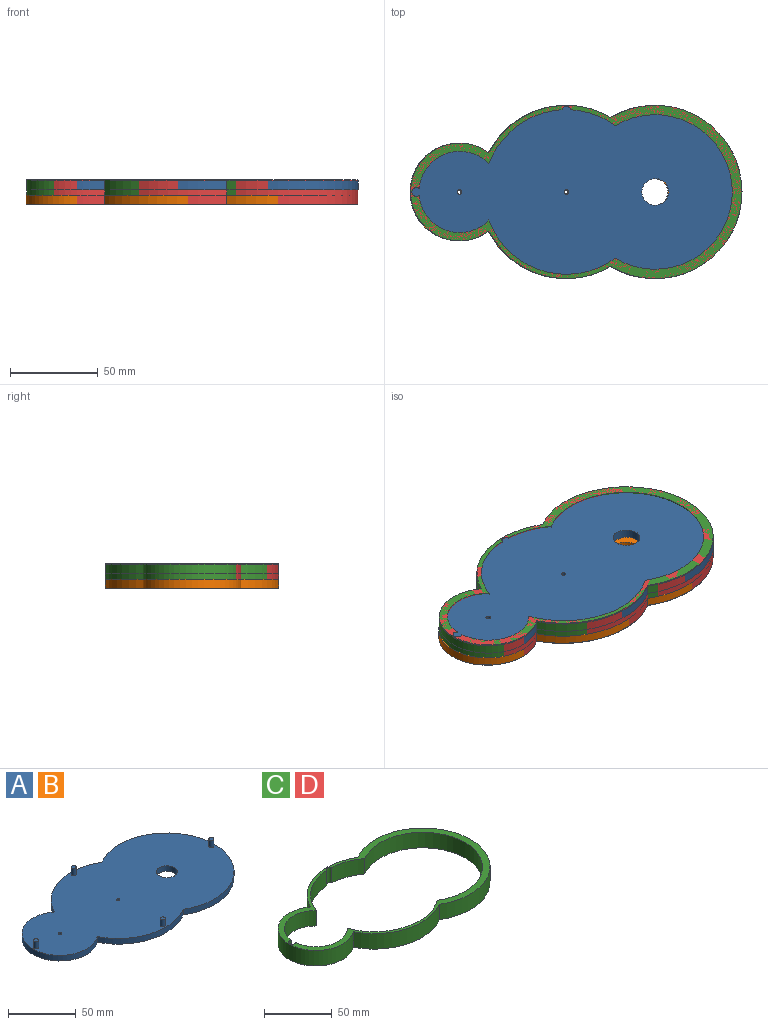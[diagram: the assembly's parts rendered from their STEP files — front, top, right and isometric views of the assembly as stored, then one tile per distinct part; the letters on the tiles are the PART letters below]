
ASSEMBLY  parts=4 mates=1
PART A: 17 faces, bbox 189.2x99.1x11.4 mm
  f0: cylinder r=27.94mm len=55.88mm, axis (0,0,-1), area 628.5mm2, adj f1,f6,f7,f8
  f1: cylinder r=49.53mm len=69.6mm, axis (0,0,-1), area 412.9mm2, adj f0,f2,f7,f8
  f2: cylinder r=49.53mm len=99.06mm, axis (0,0,-1), area 1061.4mm2, adj f1,f6,f7,f8
  f3: cylinder r=7.62mm len=15.24mm, axis (0,0,-1), area 243.2mm2, adj f7,f8
  f4: cylinder r=1.27mm len=5.08mm, axis (0,0,-1), area 40.5mm2, adj f7,f8
  f5: cylinder r=1.27mm len=5.08mm, axis (0,0,-1), area 40.5mm2, adj f7,f8
  f6: cylinder r=49.53mm len=69.6mm, axis (0,0,-1), area 412.9mm2, adj f0,f2,f7,f8
  f7: plane 189.23x99.06mm, normal (0,0,1), area 14213.4mm2, adj f0,f1,f2,f3,f4,f5,f6,f9
  f8: plane 189.23x99.06mm, normal (0,0,-1), area 14259mm2, adj f0,f1,f2,f3,f4,f5,f6
  f9: cylinder r=1.91mm len=6.35mm, axis (0,0,-1), area 76mm2, adj f7,f10
  f10: plane 3.81x3.81mm, normal (0,0,1), area 11.4mm2, adj f9
  f11: cylinder r=1.91mm len=6.35mm, axis (0,0,-1), area 76mm2, adj f7,f12
  f12: plane 3.81x3.81mm, normal (0,0,1), area 11.4mm2, adj f11
  f13: cylinder r=1.91mm len=6.35mm, axis (0,0,-1), area 76mm2, adj f7,f14
  f14: plane 3.81x3.81mm, normal (0,0,1), area 11.4mm2, adj f13
  f15: cylinder r=1.91mm len=6.35mm, axis (0,0,-1), area 76mm2, adj f7,f16
  f16: plane 3.81x3.81mm, normal (0,0,1), area 11.4mm2, adj f15
PART B: same geometry as A
PART C: 14 faces, bbox 189.2x99.1x14 mm
  f0: cylinder r=49.53mm len=69.6mm, axis (0,0,-1), area 1135.5mm2, adj f1,f11,f12,f13
  f1: cylinder r=27.94mm len=55.88mm, axis (0,0,-1), area 1728.5mm2, adj f0,f2,f12,f13
  f2: cylinder r=49.53mm len=69.6mm, axis (0,0,-1), area 1135.5mm2, adj f1,f11,f12,f13
  f3: cylinder r=47.03mm len=72.17mm, axis (0,0,-1), area 1221.9mm2, adj f4,f10,f12,f13
  f4: cylinder r=23.18mm len=39.86mm, axis (0,0,-1), area 743.6mm2, adj f3,f5,f12,f13
  f5: cylinder r=2.54mm len=13.97mm, axis (0,0,-1), area 162.1mm2, adj f4,f6,f12,f13
  f6: cylinder r=23.18mm len=39.86mm, axis (0,0,-1), area 743.6mm2, adj f5,f7,f12,f13
  f7: cylinder r=47.03mm len=41.76mm, axis (0,0,-1), area 769.5mm2, adj f6,f8,f12,f13
  f8: cylinder r=2.54mm len=13.97mm, axis (0,0,-1), area 94.2mm2, adj f7,f9,f12,f13
  f9: cylinder r=47.03mm len=25.47mm, axis (0,0,-1), area 383.5mm2, adj f8,f10,f12,f13
  f10: cylinder r=44.13mm len=88.25mm, axis (0,0,-1), area 2603mm2, adj f3,f9,f12,f13
  f11: cylinder r=49.53mm len=99.06mm, axis (0,0,-1), area 2918.9mm2, adj f0,f2,f12,f13
  f12: plane 189.23x99.06mm, normal (0,0,1), area 2031.9mm2, adj f0,f1,f2,f3,f4,f5,f6,f7
  f13: plane 189.23x99.06mm, normal (0,0,-1), area 2031.9mm2, adj f0,f1,f2,f3,f4,f5,f6,f7
PART D: same geometry as C
PLACE A rot(axis=(1,0,0),180deg) t=(56.71,152.87,29.64)mm
PLACE B t=(56.29,150.63,16.31)mm
PLACE C t=(142.44,309.81,16.31)mm
PLACE D t=(142.44,309.81,16.31)mm
MATE slider A.f13 <-> D.f8  axis (0,0,1) through (96.86,198.11,18.21)mm
